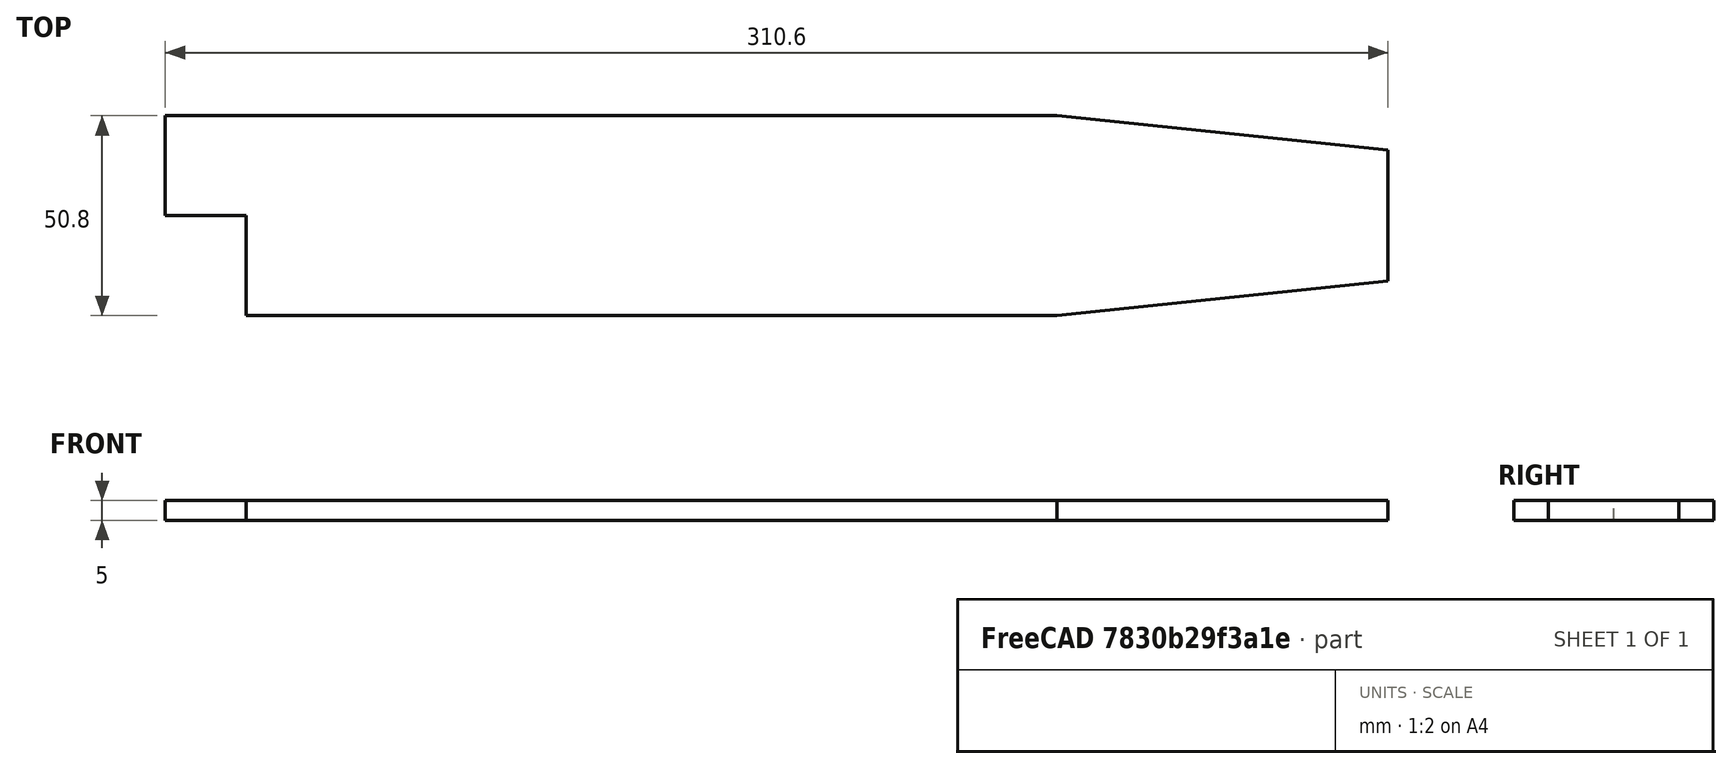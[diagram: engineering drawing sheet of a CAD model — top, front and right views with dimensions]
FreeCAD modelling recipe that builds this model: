
FCSTD DOCUMENT  (FreeCAD 1.0R39109 (Git))
Label: Pitz_Daily_N1
License: All rights reserved
LicenseURL: https://en.wikipedia.org/wiki/All_rights_reserved
objects: Sketcher::SketchObject×1, PartDesign::Pad×1, PartDesign::Body×1
note: 6 computed .brp shape members not serialized (recipe doc carries the construction recipe); baked Part::Feature solids carry a one-line shape summary decoded from their .brp

FEATURE [Sketcher::SketchObject] Sketch
  ArcFitTolerance = 1e-06
  AttachmentSupport = -> [XY_Plane]
  FullyConstrained = true
  MakeInternals = false
  MapMode = 5
  sketch-geometry (8):
    g0: LineSegment StartX=0 StartY=25.4 StartZ=0 EndX=20.6 EndY=25.4 EndZ=0
    g1: LineSegment StartX=20.6 StartY=25.4 StartZ=0 EndX=20.6 EndY=0 EndZ=0
    g2: LineSegment StartX=20.6 StartY=0 StartZ=0 EndX=226.6 EndY=0 EndZ=0
    g3: LineSegment StartX=0 StartY=25.4 StartZ=0 EndX=0 EndY=50.8 EndZ=0
    g4: LineSegment StartX=0 StartY=50.8 StartZ=0 EndX=226.6 EndY=50.8 EndZ=0
    g5: LineSegment StartX=226.6 StartY=50.8 StartZ=0 EndX=310.6 EndY=42 EndZ=0
    g6: LineSegment StartX=226.6 StartY=0 StartZ=0 EndX=310.6 EndY=8.8 EndZ=0
    g7: LineSegment StartX=310.6 StartY=42 StartZ=0 EndX=310.6 EndY=8.8 EndZ=0
  constraints (23):
    c: Distance(g0) = 20.6
    c: Horizontal(g0)
    c: PointOnObject(g0,g-2)
    c: Coincident(g1,g0)
    c: Perpendicular(g0,g1)
    c: Distance(g2) = 206
    c: Coincident(g2,g1)
    c: DistanceY(g1,g1) = 25.4
    c: Distance(g3) = 25.4
    c: Vertical(g3)
    c: Coincident(g3,g0)
    c: Distance(g4) = 226.6
    c: Horizontal(g4)
    c: Coincident(g4,g3)
    c: Coincident(g5,g4)
    c: DistanceX(g5,g5) = 84
    c: Vertical(g6,g5)
    c: Coincident(g6,g2)
    c: DistanceY(g6,g5) = 33.2
    c: DistanceY(g6,g6) = 8.8
    c: Coincident(g7,g5)
    c: Coincident(g7,g6)
    c: Tangent(g2,g-1)
FEATURE [PartDesign::Pad] Pad
  Direction = (0,0,1)
  Length = 5
  Length2 = 10
  Midplane = true
  Profile = -> Sketch
  ReferenceAxis = -> Sketch [N_Axis]
  Refine = true
  Suppressed = false
  Type = 0
FEATURE [PartDesign::Body] Body  label="Cuerpo"
  AllowCompound = false
  Group = -> [Sketch,Pad]
  Origin = -> Origin
  Tip = -> Pad
